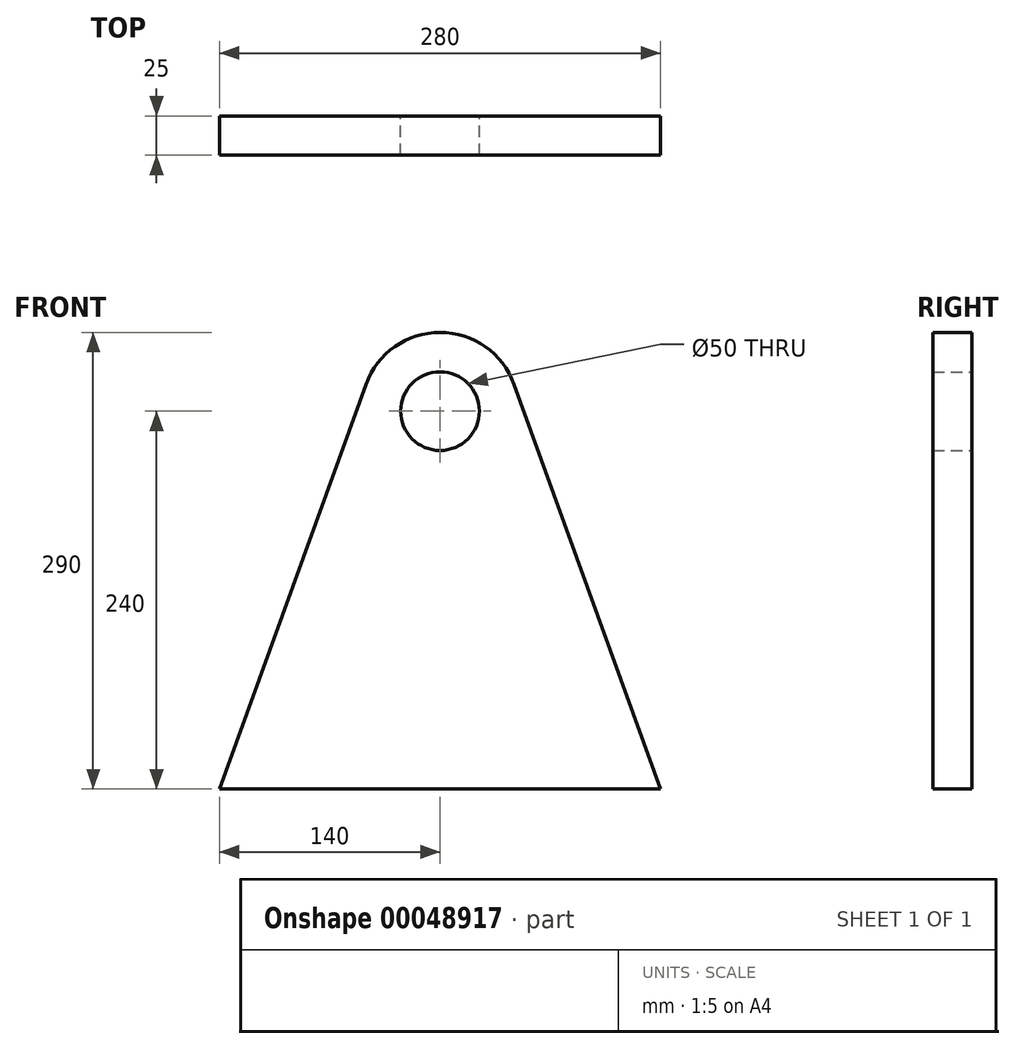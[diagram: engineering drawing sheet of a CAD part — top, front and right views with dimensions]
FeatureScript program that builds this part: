
annotation { "Feature Type Name" : "Feature", "Feature Type Description" : "" }
export const myFeature = defineFeature(function(context is Context, id is Id, definition is map)
    precondition{}
    {
        {
            var Q0;
            Q0=qCreatedBy(makeId("Front.planeOp"),FACE);
            var sketch = newSketch(context, id + "F0", { "sketchPlane" : qUnion([Q0])});
            skCircle(sketch, "E0", {"center": v(0, 0) * mm, "radius": 25 * mm});
            skCircle(sketch, "E1", {"center": v(0, 0) * mm, "radius": 50 * mm});
            skLineSegment(sketch, "E2", {"start": v(0, 0) * mm, "end": v(0, -240) * mm, "construction": true});
            skLineSegment(sketch, "E3", {"start": v(0, -240) * mm, "end": v(-140, -240) * mm});
            skLineSegment(sketch, "E4", {"start": v(0, -240) * mm, "end": v(140, -240) * mm});
            skLineSegment(sketch, "E5", {"start": v(-140, -240) * mm, "end": v(-44.15, 24.94) * mm});
            skLineSegment(sketch, "E6", {"start": v(140, -240) * mm, "end": v(43.08, 27.9) * mm});
            skSolve(sketch);
        }
        {
            var Q0;
            {var subQ6=sQuery(id+"F0.wireOp",EDGE,"E3");Q0=makeQuery(id+"F0.imprint","IMPRINT",FACE,{"disambiguationData":[TD([[makeQuery(id+"F0.imprint","IMPRINT",EDGE,{"derivedFrom":subQ6}),-1.0]])]});}
            var Q1;
            Q1=makeQuery(id+"F0.imprint","IMPRINT",FACE,{"disambiguationData":[TD([[makeQuery(id+"F0.imprint","IMPRINT",EDGE,{"derivedFrom":sQuery(id+"F0.wireOp",EDGE,"E0")}),-1.0]])]});
            extrude(context, id + "F1", {"entities" : qUnion([Q0, Q1]), "depth" : 25 * mm});
        }
    });
